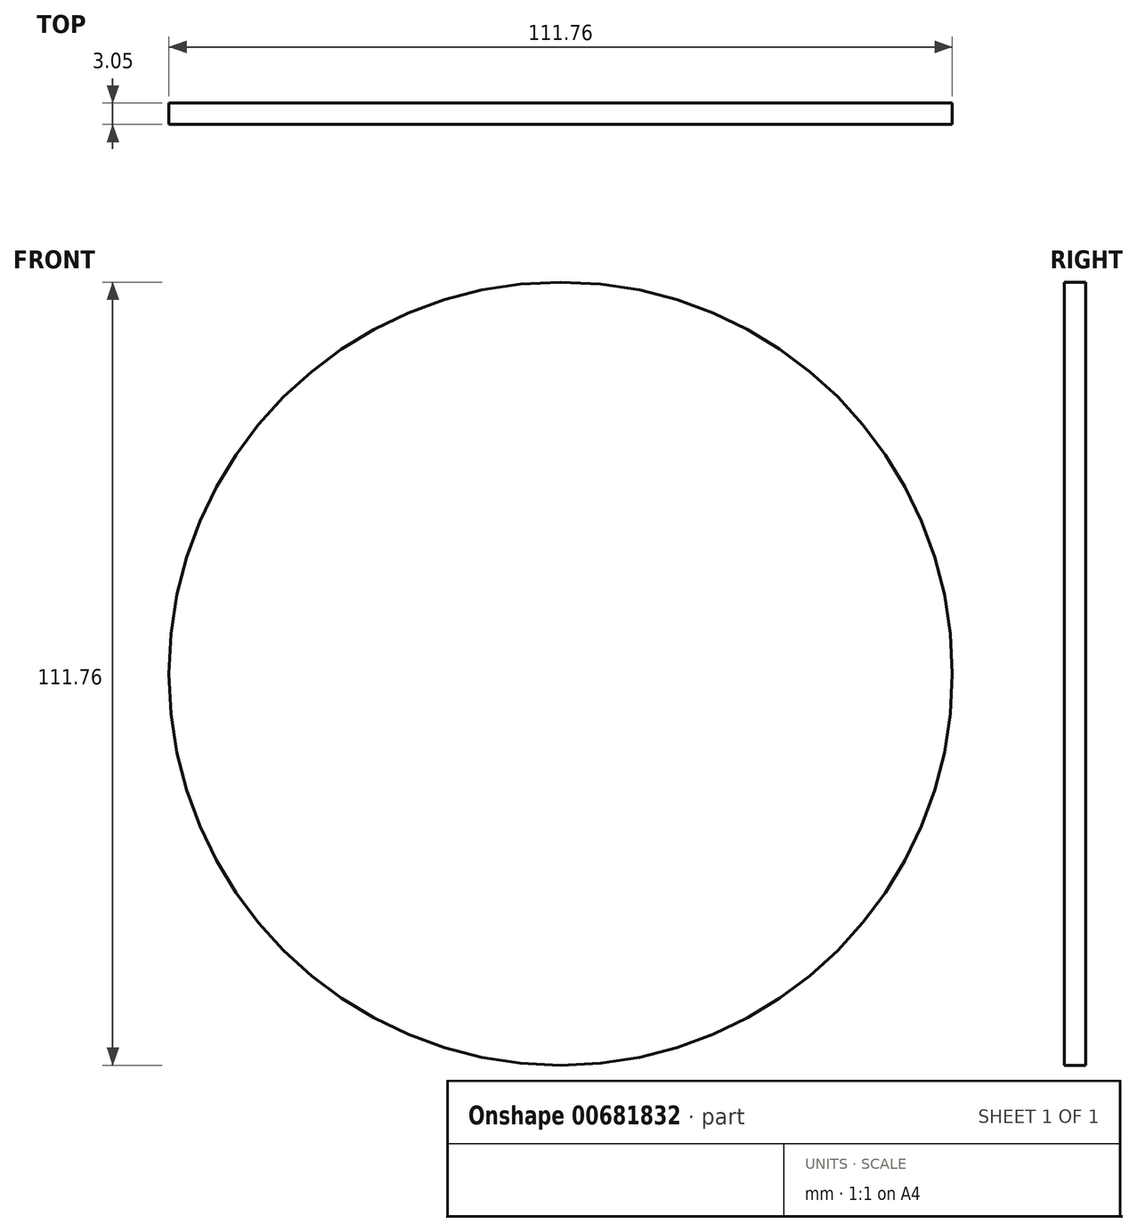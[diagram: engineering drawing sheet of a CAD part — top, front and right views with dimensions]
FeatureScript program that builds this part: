
annotation { "Feature Type Name" : "Feature", "Feature Type Description" : "" }
export const myFeature = defineFeature(function(context is Context, id is Id, definition is map)
    precondition{}
    {
        {
            var Q0;
            Q0=qCreatedBy(makeId("Front.planeOp"),FACE);
            var sketch = newSketch(context, id + "F0", { "sketchPlane" : qUnion([Q0])});
            skCircle(sketch, "E0", {"center": v(0, 0) * mm, "radius": 55.88 * mm});
            skArc(sketch, "E1", {"start": v(-40.26, 38.75) * mm, "mid": v(0, 55.88) * mm, "end": v(40.25, 38.77) * mm});
            skCircle(sketch, "E2", {"center": v(0.03, 0.02) * mm, "radius": 10.67 * mm});
            skSolve(sketch);
        }
        {
            var Q0;
            Q0=makeQuery(id+"F0.imprint","IMPRINT",FACE,{"disambiguationData":[TD([[makeQuery(id+"F0.imprint","IMPRINT",EDGE,{"derivedFrom":sQuery(id+"F0.wireOp",EDGE,"E0")}),1.0]])]});
            var Q1;
            Q1=makeQuery(id+"F0.imprint","IMPRINT",FACE,{"disambiguationData":[TD([[makeQuery(id+"F0.imprint","IMPRINT",EDGE,{"derivedFrom":sQuery(id+"F0.wireOp",EDGE,"a0dda0ec-a6f0-444d-9fac-eba678589948.bottom")}),-1.0]])]});
            var Q2;
            {var subQ0=sQuery(id+"F0.wireOp",EDGE,"a0dda0ec-a6f0-444d-9fac-eba678589948.top");var subQ1=sQuery(id+"F0.wireOp",EDGE,"5fc55c55-048c-439b-975f-e61c214eae0e");var subQ2=makeQuery(id+"F0.imprint","INTERSECT",VERTEX,{"disambiguationData":[OD(0.0)],"derivedFrom":[subQ1,subQ0]});Q2=makeQuery(id+"F0.imprint","IMPRINT",FACE,{"disambiguationData":[TD([[makeQuery(id+"F0.imprint","IMPRINT",EDGE,{"disambiguationData":[TD([[subQ2,1.0]])],"derivedFrom":subQ1}),1.0]])]});}
            var Q3;
            Q3=makeQuery(id+"F0.imprint","IMPRINT",FACE,{"disambiguationData":[TD([[makeQuery(id+"F0.imprint","IMPRINT",EDGE,{"derivedFrom":sQuery(id+"F0.wireOp",EDGE,"770fa09b-950f-4902-a980-98a33f02e4e5.bottom")}),-1.0]])]});
            var Q4;
            {var subQ0=sQuery(id+"F0.wireOp",EDGE,"770fa09b-950f-4902-a980-98a33f02e4e5.top");var subQ1=sQuery(id+"F0.wireOp",EDGE,"E2");var subQ2=makeQuery(id+"F0.imprint","INTERSECT",VERTEX,{"disambiguationData":[OD(0.0)],"derivedFrom":[subQ1,subQ0]});Q4=makeQuery(id+"F0.imprint","IMPRINT",FACE,{"disambiguationData":[TD([[makeQuery(id+"F0.imprint","IMPRINT",EDGE,{"disambiguationData":[TD([[subQ2,1.0]])],"derivedFrom":subQ1}),1.0]])]});}
            extrude(context, id + "F1", {"entities" : qUnion([Q0, Q1, Q2, Q3, Q4]), "depth" : 3.05 * mm, "offsetDistance" : 25.4 * mm});
        }
    });
